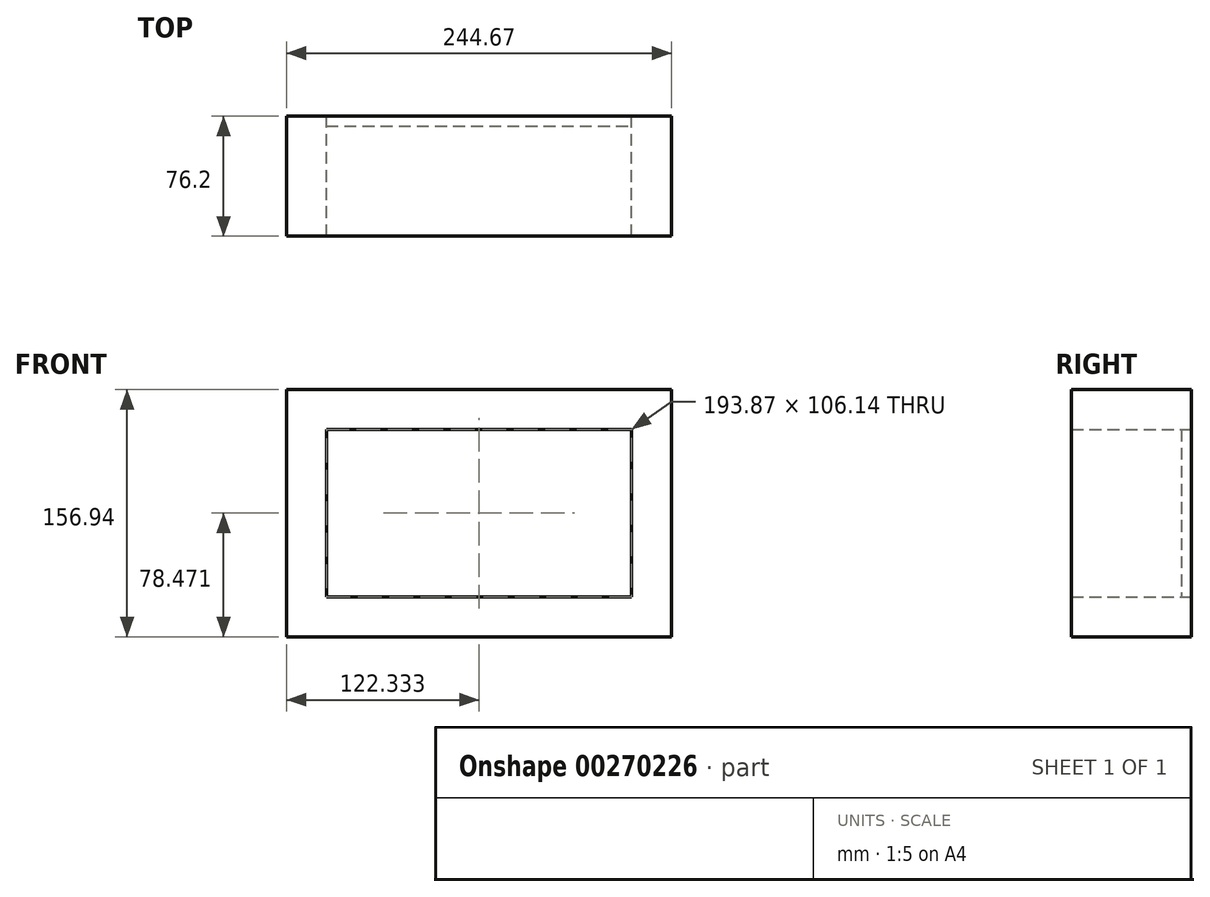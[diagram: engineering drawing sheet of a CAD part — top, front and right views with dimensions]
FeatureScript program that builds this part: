
annotation { "Feature Type Name" : "Feature", "Feature Type Description" : "" }
export const myFeature = defineFeature(function(context is Context, id is Id, definition is map)
    precondition{}
    {
        {
            var Q0;
            Q0=qCreatedBy(makeId("Front.planeOp"),FACE);
            var sketch = newSketch(context, id + "F0", { "sketchPlane" : qUnion([Q0])});
            skLineSegment(sketch, "E0.bottom", {"start": v(-96.7, 48.5) * mm, "end": v(97.18, 48.5) * mm});
            skLineSegment(sketch, "E0.top", {"start": v(-96.7, -57.64) * mm, "end": v(97.18, -57.64) * mm});
            skLineSegment(sketch, "E0.left", {"start": v(-96.7, 48.5) * mm, "end": v(-96.7, -57.64) * mm});
            skLineSegment(sketch, "E0.right", {"start": v(97.18, 48.5) * mm, "end": v(97.18, -57.64) * mm});
            skLineSegment(sketch, "E1.bottom", {"start": v(-122.1, 73.9) * mm, "end": v(122.58, 73.9) * mm});
            skLineSegment(sketch, "E1.top", {"start": v(-122.1, -83.04) * mm, "end": v(122.58, -83.04) * mm});
            skLineSegment(sketch, "E1.left", {"start": v(-122.1, 73.9) * mm, "end": v(-122.1, -83.04) * mm});
            skLineSegment(sketch, "E1.right", {"start": v(122.58, 73.9) * mm, "end": v(122.58, -83.04) * mm});
            skSolve(sketch);
        }
        {
            var Q0;
            Q0=makeQuery(id+"F0.imprint","IMPRINT",FACE,{"disambiguationData":[TD([[makeQuery(id+"F0.imprint","IMPRINT",EDGE,{"derivedFrom":sQuery(id+"F0.wireOp",EDGE,"E0.bottom")}),-1.0]])]});
            extrude(context, id + "F1", {"entities" : qUnion([Q0]), "depth" : 6.35 * mm});
        }
        {
            var Q0;
            Q0=makeQuery(id+"F0.imprint","IMPRINT",FACE,{"disambiguationData":[TD([[makeQuery(id+"F0.imprint","IMPRINT",EDGE,{"derivedFrom":sQuery(id+"F0.wireOp",EDGE,"E0.bottom")}),1.0]])]});
            extrude(context, id + "F2", {"entities" : qUnion([Q0]), "depth" : 76.2 * mm});
        }
    });
